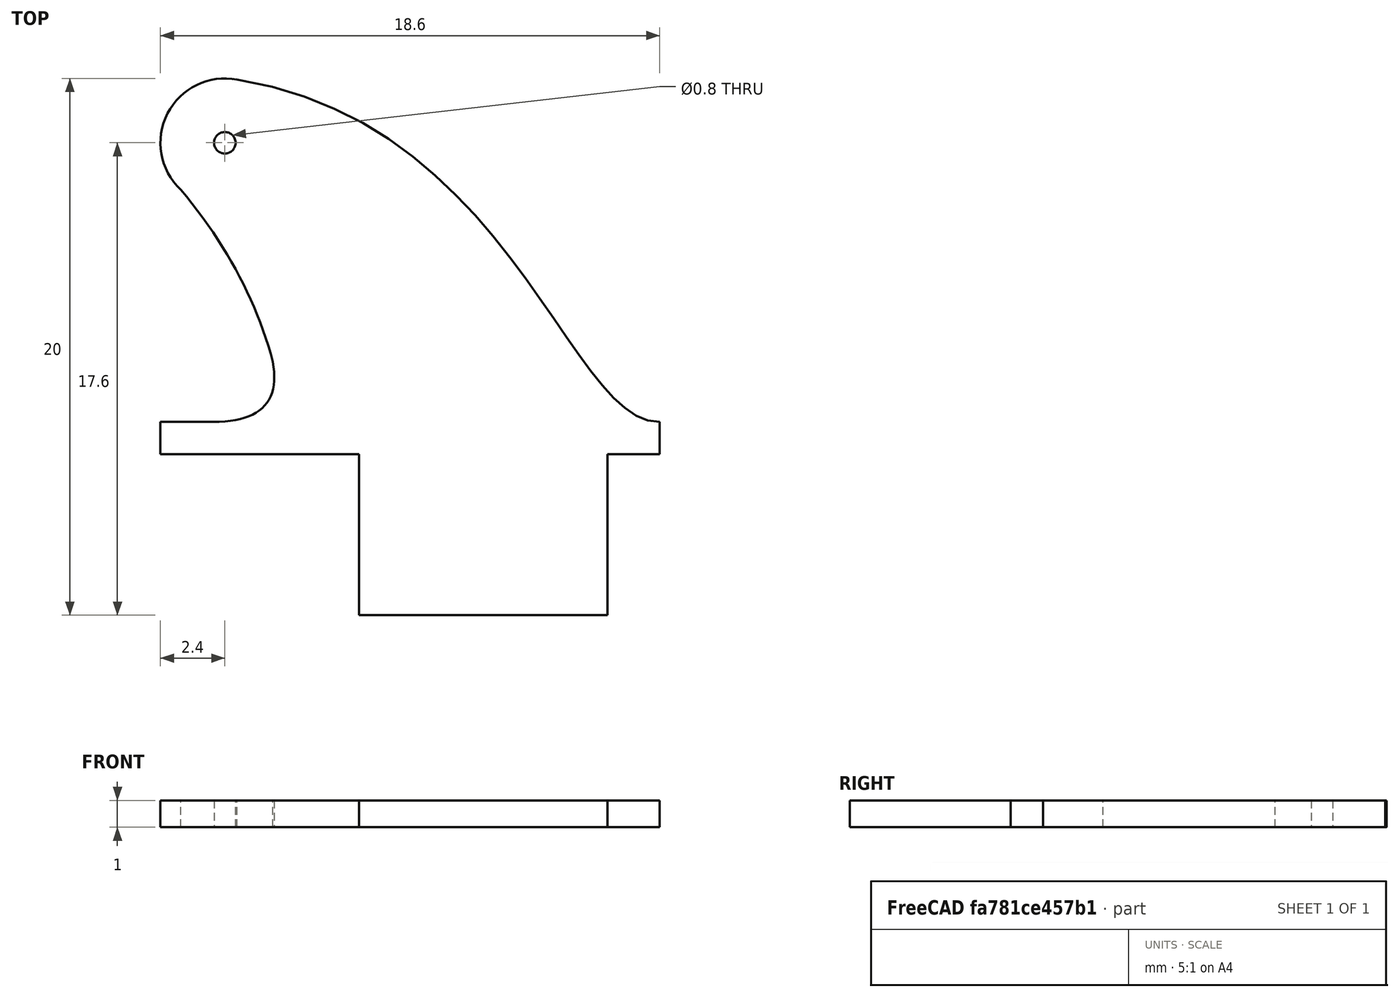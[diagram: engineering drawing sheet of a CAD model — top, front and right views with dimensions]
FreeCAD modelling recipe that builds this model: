
FCSTD DOCUMENT  (FreeCAD 0.20R0.20.2)
Label: 006
License: All rights reserved
LicenseURL: http://en.wikipedia.org/wiki/All_rights_reserved
objects: Sketcher::SketchObject×2, Part::Extrusion×1
note: 3 computed .brp shape members not serialized (recipe doc carries the construction recipe); baked Part::Feature solids carry a one-line shape summary decoded from their .brp

FEATURE [Sketcher::SketchObject] Sketch  label="main"
  FullyConstrained = true
  sketch-geometry (25):
    g0: LineSegment StartX=12.0586 StartY=-6 StartZ=0 EndX=12.0586 EndY=0 EndZ=0
    g1: LineSegment StartX=2.8 StartY=-6 StartZ=0 EndX=2.8 EndY=0 EndZ=0
    g2: LineSegment StartX=2.8 StartY=-6 StartZ=0 EndX=12.0586 EndY=-6 EndZ=0
    g3: LineSegment StartX=12.0586 StartY=0 StartZ=0 EndX=14 EndY=0 EndZ=0
    g4: LineSegment StartX=2.8 StartY=0 StartZ=0 EndX=0 EndY=0 EndZ=0
    g5: LineSegment StartX=14 StartY=0 StartZ=0 EndX=14 EndY=1.2 EndZ=0
    g6: LineSegment StartX=0 StartY=0 StartZ=0 EndX=-4.6 EndY=0 EndZ=0
    g7: Circle CenterX=-2.2 CenterY=11.6 CenterZ=0 NormalX=0 NormalY=0 NormalZ=1 AngleXU=0 Radius=0.4
    g8-g11: Circle x4 (B-spline internal-alignment scaffolding for g12; pole/knot coordinates omitted)
    g12: BSplineCurve PolesCount=4 KnotsCount=2 Degree=3 IsPeriodic=0
    g13: GeomPoint X=-1.74436 Y=13.9564 Z=0
    g14: GeomPoint X=14 Y=1.2 Z=0
    g15: ArcOfCircle CenterX=-2.2 CenterY=11.6 CenterZ=0 NormalX=0 NormalY=0 NormalZ=1 AngleXU=0 Radius=2.4 StartAngle=1.37979 EndAngle=3.95565
    g16: LineSegment StartX=-2.62672 StartY=1.2 StartZ=0 EndX=-4.6 EndY=1.2 EndZ=0
    g17: LineSegment StartX=-4.6 StartY=0 StartZ=0 EndX=-4.6 EndY=1.2 EndZ=0
    g18: Circle CenterX=-2.62672 CenterY=1.2 CenterZ=0 NormalX=0 NormalY=0 NormalZ=1 AngleXU=0 Radius=1
    g19: Circle CenterX=0 CenterY=1.2 CenterZ=0 NormalX=0 NormalY=0 NormalZ=1 AngleXU=0 Radius=1
    g20: Circle CenterX=-0.413885 CenterY=3.44541 CenterZ=0 NormalX=0 NormalY=0 NormalZ=1 AngleXU=0 Radius=1
    g21: BSplineCurve PolesCount=3 KnotsCount=2 Degree=2 IsPeriodic=0
    g22: GeomPoint X=-2.62672 Y=1.2 Z=0
    g23: GeomPoint X=-0.413885 Y=3.44541 Z=0
    g24: BSplineCurve PolesCount=3 KnotsCount=2 Degree=2 IsPeriodic=0
  constraints (52):
    c: Vertical(g0)
    c: Vertical(g1)
    c: Block(g1)
    c: Block(g0)
    c: Distance(g1) = 6
    c: Coincident(g2,g1)
    c: Horizontal(g2)
    c: Coincident(g0,g2)
    c: Block(g2)
    c: Coincident(g3,g0)
    c: Horizontal(g3)
    c: Coincident(g4,g1)
    c: Horizontal(g4)
    c: Block(g3)
    c: Block(g4)
    c: Coincident(g5,g3)
    c: Vertical(g5)
    c: Distance(g5) = 1.2
    c: Coincident(g6,g4)
    c: Horizontal(g6)
    c: Distance(g6) = 4.6
    c: Block(g7)
    c: Weight(g8) = 1
    c: Equal(g8,g9)
    c: Equal(g8,g10)
    c: Equal(g8,g11)
    c: Coincident(g12,g5)
    c: InternalAlignment(g8-g11 -> g12) x4
    c: InternalAlignment(g13,g12)
    c: InternalAlignment(g14,g12)
    c: Block(g12)
    c: Coincident(g15,g7)
    c: Coincident(g15,g12)
    c: Coincident(g15,g24)
    c: Block(g15)
    c: Horizontal(g16)
    c: Coincident(g17,g6)
    c: Vertical(g17)
    c: Coincident(g17,g16)
    c: Weight(g18) = 1
    c: Equal(g18,g19)
    c: Equal(g18,g20)
    c: InternalAlignment(g18,g21)
    c: InternalAlignment(g19,g21)
    c: InternalAlignment(g20,g21)
    c: InternalAlignment(g22,g21)
    c: InternalAlignment(g23,g21)
    c: Block(g16)
    c: Coincident(g16,g21)
    c: Coincident(g21,g24)
    c: Block(g24)
    c: Block(g21)
FEATURE [Part::Extrusion] Extrude
  Base = -> Sketch
  Dir = (0,0,1)
  DirMode = 2
  FaceMakerClass = Part::FaceMakerBullseye
  LengthFwd = 1
  LengthRev = 0
  Solid = true
  Symmetric = false
FEATURE [Sketcher::SketchObject] Sketch001  label="main001"
  FullyConstrained = true
  sketch-geometry (48):
    g0: LineSegment StartX=12.0586 StartY=-6 StartZ=0 EndX=12.0586 EndY=0 EndZ=0
    g1: LineSegment StartX=2.8 StartY=-6 StartZ=0 EndX=2.8 EndY=0 EndZ=0
    g2: LineSegment StartX=2.8 StartY=-6 StartZ=0 EndX=12.0586 EndY=-6 EndZ=0
    g3: LineSegment StartX=12.0586 StartY=0 StartZ=0 EndX=14 EndY=0 EndZ=0
    g4: LineSegment StartX=2.8 StartY=0 StartZ=0 EndX=0 EndY=0 EndZ=0
    g5: LineSegment StartX=14 StartY=0 StartZ=0 EndX=14 EndY=1.2 EndZ=0
    g6: LineSegment StartX=0 StartY=0 StartZ=0 EndX=-4.6 EndY=0 EndZ=0
    g7: Circle CenterX=-2.2 CenterY=11.6 CenterZ=0 NormalX=0 NormalY=0 NormalZ=1 AngleXU=0 Radius=0.4
    g8-g11: Circle x4 (B-spline internal-alignment scaffolding for g12; pole/knot coordinates omitted)
    g12: BSplineCurve PolesCount=4 KnotsCount=2 Degree=3 IsPeriodic=0
    g13: GeomPoint X=-1.74436 Y=13.9564 Z=0
    g14: GeomPoint X=14 Y=1.2 Z=0
    g15: ArcOfCircle CenterX=-2.2 CenterY=11.6 CenterZ=0 NormalX=0 NormalY=0 NormalZ=1 AngleXU=0 Radius=2.4 StartAngle=1.37979 EndAngle=3.95565
    g16: LineSegment StartX=-2.62672 StartY=1.2 StartZ=0 EndX=-4.6 EndY=1.2 EndZ=0
    g17: LineSegment StartX=-4.6 StartY=0 StartZ=0 EndX=-4.6 EndY=1.2 EndZ=0
    g18: Circle CenterX=-2.62672 CenterY=1.2 CenterZ=0 NormalX=0 NormalY=0 NormalZ=1 AngleXU=0 Radius=1
    g19: Circle CenterX=0 CenterY=1.2 CenterZ=0 NormalX=0 NormalY=0 NormalZ=1 AngleXU=0 Radius=1
    g20: Circle CenterX=-0.413885 CenterY=3.44541 CenterZ=0 NormalX=0 NormalY=0 NormalZ=1 AngleXU=0 Radius=1
    g21: BSplineCurve PolesCount=3 KnotsCount=2 Degree=2 IsPeriodic=0
    g22: GeomPoint X=-2.62672 Y=1.2 Z=0
    g23: GeomPoint X=-0.413885 Y=3.44541 Z=0
    g24: BSplineCurve PolesCount=3 KnotsCount=2 Degree=2 IsPeriodic=0
    g25: LineSegment StartX=-2.2 StartY=11.6 StartZ=0 EndX=-0.6 EndY=11.6 EndZ=0
    g26: Circle CenterX=-2.2 CenterY=11.6 CenterZ=0 NormalX=0 NormalY=0 NormalZ=1 AngleXU=0 Radius=1.6
    g27: LineSegment StartX=0 StartY=1.2 StartZ=0 EndX=1.34801 EndY=2.51783 EndZ=0
    g28: LineSegment StartX=-0.413885 StartY=3.44541 StartZ=0 EndX=-0.249951 EndY=7.1888 EndZ=0
    g29: Circle CenterX=-3.3091 CenterY=10.4468 CenterZ=0 NormalX=0 NormalY=0 NormalZ=1 AngleXU=0 Radius=1
    g30: Circle CenterX=-0.249951 CenterY=7.1888 CenterZ=0 NormalX=0 NormalY=0 NormalZ=1 AngleXU=0 Radius=1
    g31: Circle CenterX=1.34801 CenterY=2.51783 CenterZ=0 NormalX=0 NormalY=0 NormalZ=1 AngleXU=0 Radius=1
    g32: BSplineCurve PolesCount=3 KnotsCount=2 Degree=2 IsPeriodic=0
    g33: GeomPoint X=-3.3091 Y=10.4468 Z=0
    g34: GeomPoint X=1.34801 Y=2.51783 Z=0
    g35: LineSegment StartX=0 StartY=1.2 StartZ=0 EndX=3.28198 EndY=1.2 EndZ=0
    g36: Circle CenterX=1.34801 CenterY=2.51783 CenterZ=0 NormalX=0 NormalY=0 NormalZ=1 AngleXU=0 Radius=1
    g37: Circle CenterX=1.8831 CenterY=1.2 CenterZ=0 NormalX=0 NormalY=0 NormalZ=1 AngleXU=0 Radius=1
    g38: Circle CenterX=3.28198 CenterY=1.2 CenterZ=0 NormalX=0 NormalY=0 NormalZ=1 AngleXU=0 Radius=1
    g39: BSplineCurve PolesCount=3 KnotsCount=2 Degree=2 IsPeriodic=0
    g40: GeomPoint X=1.34801 Y=2.51783 Z=0
    g41: GeomPoint X=3.28198 Y=1.2 Z=0
    g42: Circle CenterX=-1.79622 CenterY=13.1482 CenterZ=0 NormalX=0 NormalY=0 NormalZ=1 AngleXU=0 Radius=1
    g43: Circle CenterX=4.68963 CenterY=11.6896 CenterZ=0 NormalX=0 NormalY=0 NormalZ=1 AngleXU=0 Radius=1
    g44: Circle CenterX=9.22372 CenterY=2.86164 CenterZ=0 NormalX=0 NormalY=0 NormalZ=1 AngleXU=0 Radius=1
    g45: BSplineCurve PolesCount=3 KnotsCount=2 Degree=2 IsPeriodic=0
    g46: GeomPoint X=-1.79622 Y=13.1482 Z=0
    g47: GeomPoint X=9.22372 Y=2.86164 Z=0
  constraints (94):
    c: Vertical(g0)
    c: Vertical(g1)
    c: Block(g1)
    c: Block(g0)
    c: Distance(g1) = 6
    c: Coincident(g2,g1)
    c: Horizontal(g2)
    c: Coincident(g0,g2)
    c: Block(g2)
    c: Coincident(g3,g0)
    c: Horizontal(g3)
    c: Coincident(g4,g1)
    c: Horizontal(g4)
    c: Block(g3)
    c: Block(g4)
    c: Coincident(g5,g3)
    c: Vertical(g5)
    c: Distance(g5) = 1.2
    c: Coincident(g6,g4)
    c: Horizontal(g6)
    c: Distance(g6) = 4.6
    c: Block(g7)
    c: Weight(g8) = 1
    c: Equal(g8,g9)
    c: Equal(g8,g10)
    c: Equal(g8,g11)
    c: Coincident(g12,g5)
    c: InternalAlignment(g8-g11 -> g12) x4
    c: InternalAlignment(g13,g12)
    c: InternalAlignment(g14,g12)
    c: Block(g12)
    c: Coincident(g15,g7)
    c: Coincident(g15,g12)
    c: Coincident(g15,g24)
    c: Block(g15)
    c: Horizontal(g16)
    c: Coincident(g17,g6)
    c: Vertical(g17)
    c: Coincident(g17,g16)
    c: Weight(g18) = 1
    c: Equal(g18,g20)
    c: InternalAlignment(g18,g21)
    c: InternalAlignment(g19,g21)
    c: InternalAlignment(g20,g21)
    c: InternalAlignment(g22,g21)
    c: InternalAlignment(g23,g21)
    c: Block(g16)
    c: Coincident(g16,g21)
    c: Coincident(g21,g24)
    c: Block(g24)
    c: Block(g21)
    c: Coincident(g25,g7)
    c: Horizontal(g25)
    c: Distance(g25) = 1.6
    c: Coincident(g26,g7)
    c: PointOnObject(g25,g26)
    c: Coincident(g27,g19)
    c: Coincident(g28,g21)
    c: Weight(g29) = 1
    c: PointOnObject(g32,g26)
    c: Equal(g29,g30)
    c: Coincident(g30,g28)
    c: Equal(g29,g31)
    c: Coincident(g32,g27)
    c: InternalAlignment(g29,g32)
    c: InternalAlignment(g30,g32)
    c: InternalAlignment(g31,g32)
    c: InternalAlignment(g33,g32)
    c: InternalAlignment(g34,g32)
    c: Block(g32)
    c: Coincident(g35,g27)
    c: Horizontal(g35)
    c: Weight(g36) = 1
    c: Coincident(g39,g27)
    c: Equal(g36,g37)
    c: PointOnObject(g37,g35)
    c: Equal(g36,g38)
    c: Coincident(g39,g35)
    c: InternalAlignment(g36,g39)
    c: InternalAlignment(g37,g39)
    c: InternalAlignment(g38,g39)
    c: InternalAlignment(g40,g39)
    c: InternalAlignment(g41,g39)
    c: Block(g39)
    c: Weight(g42) = 1
    c: PointOnObject(g45,g26)
    c: Equal(g42,g43)
    c: Equal(g42,g44)
    c: InternalAlignment(g42,g45)
    c: InternalAlignment(g43,g45)
    c: InternalAlignment(g44,g45)
    c: InternalAlignment(g46,g45)
    c: InternalAlignment(g47,g45)
    c: Block(g45)
